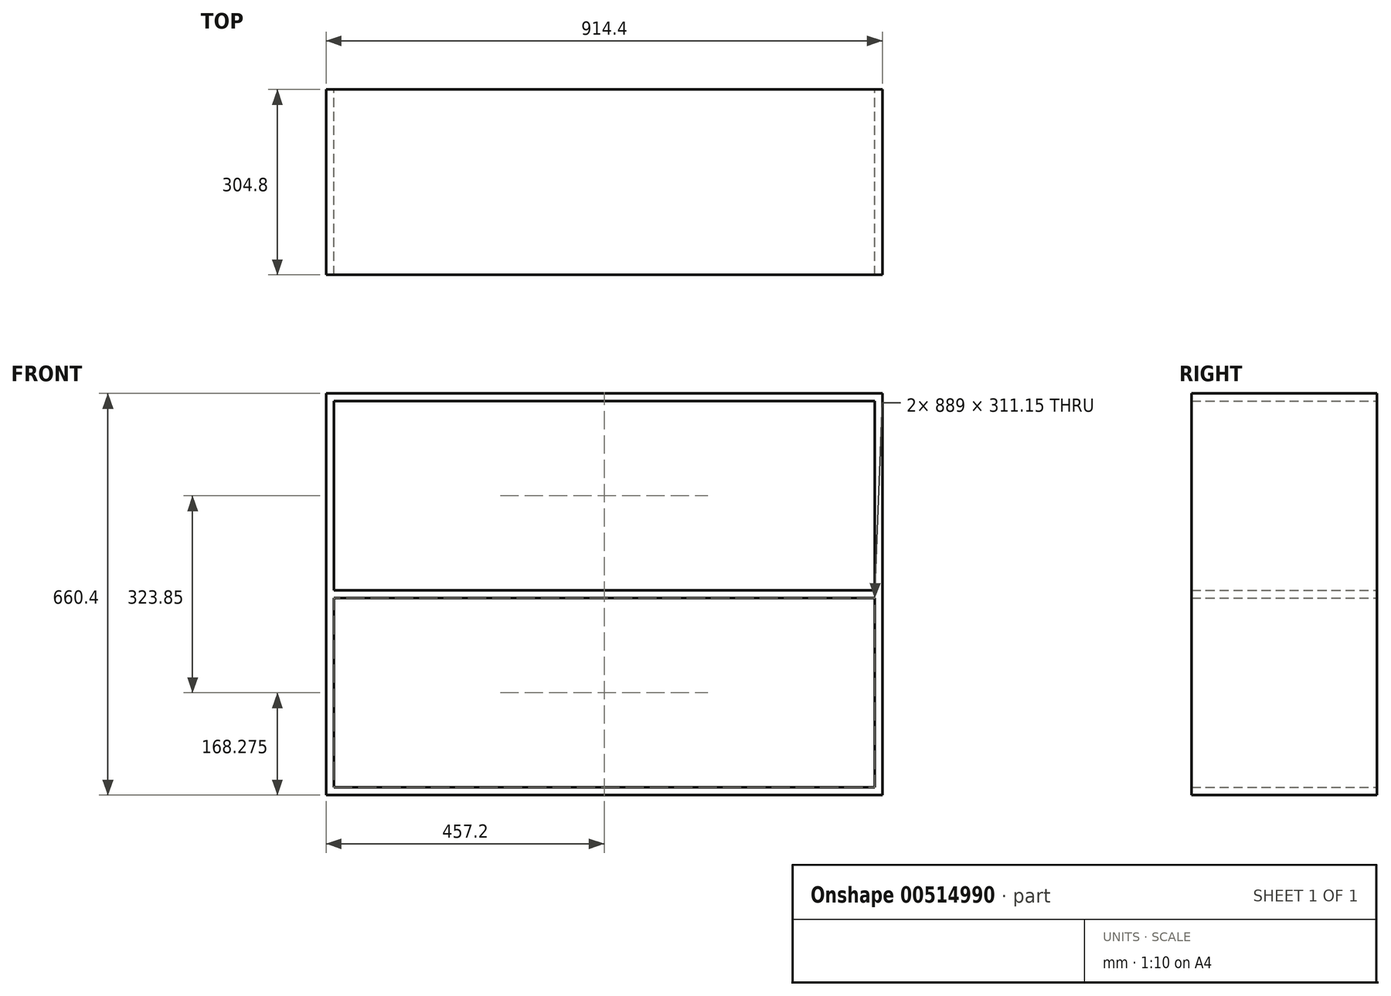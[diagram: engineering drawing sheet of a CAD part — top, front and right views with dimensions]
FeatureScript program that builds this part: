
annotation { "Feature Type Name" : "Feature", "Feature Type Description" : "" }
export const myFeature = defineFeature(function(context is Context, id is Id, definition is map)
    precondition{}
    {
        {
            var Q0;
            Q0=qCreatedBy(makeId("Front.planeOp"),FACE);
            var sketch = newSketch(context, id + "F0", { "sketchPlane" : qUnion([Q0])});
            skLineSegment(sketch, "E0.bottom", {"start": v(0, 0) * mm, "end": v(914.4, 0) * mm});
            skLineSegment(sketch, "E0.top", {"start": v(0, 660.4) * mm, "end": v(914.4, 660.4) * mm});
            skLineSegment(sketch, "E0.left", {"start": v(0, 0) * mm, "end": v(0, 660.4) * mm});
            skLineSegment(sketch, "E0.right", {"start": v(914.4, 0) * mm, "end": v(914.4, 660.4) * mm});
            skLineSegment(sketch, "E1.0", {"start": v(12.7, 323.85) * mm, "end": v(901.7, 323.85) * mm});
            skLineSegment(sketch, "E2.0", {"start": v(12.7, 336.55) * mm, "end": v(901.7, 336.55) * mm});
            skLineSegment(sketch, "E3.0", {"start": v(12.7, 12.7) * mm, "end": v(12.7, 323.85) * mm});
            skLineSegment(sketch, "E4.0", {"start": v(901.7, 12.7) * mm, "end": v(901.7, 323.85) * mm});
            skLineSegment(sketch, "E5.trimOffspring", {"start": v(12.7, 336.55) * mm, "end": v(12.7, 647.7) * mm});
            skLineSegment(sketch, "E6.trimOffspring", {"start": v(901.7, 336.55) * mm, "end": v(901.7, 647.7) * mm});
            skLineSegment(sketch, "E7.0", {"start": v(12.7, 647.7) * mm, "end": v(901.7, 647.7) * mm});
            skLineSegment(sketch, "E8.0", {"start": v(12.7, 12.7) * mm, "end": v(901.7, 12.7) * mm});
            skSolve(sketch);
        }
        {
            var Q0;
            Q0=makeQuery(id+"F0.imprint","IMPRINT",FACE,{"disambiguationData":[TD([[makeQuery(id+"F0.imprint","IMPRINT",EDGE,{"derivedFrom":sQuery(id+"F0.wireOp",EDGE,"E0.bottom")}),1.0]])]});
            extrude(context, id + "F1", {"entities" : qUnion([Q0]), "depth" : 304.8 * mm, "offsetDistance" : 25.4 * mm});
        }
    });
